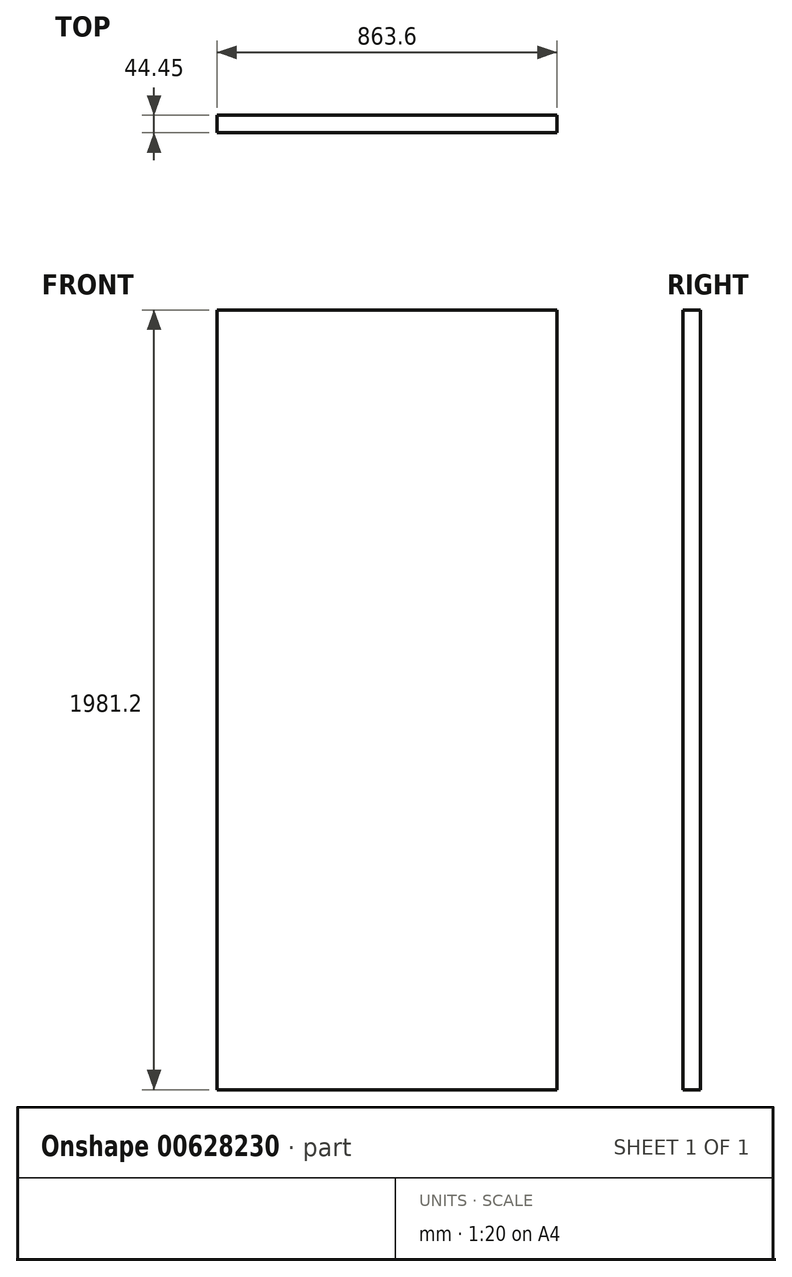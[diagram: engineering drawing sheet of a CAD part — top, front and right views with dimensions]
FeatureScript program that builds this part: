
annotation { "Feature Type Name" : "Feature", "Feature Type Description" : "" }
export const myFeature = defineFeature(function(context is Context, id is Id, definition is map)
    precondition{}
    {
        {
            var Q0;
            Q0=qCreatedBy(makeId("Front.planeOp"),FACE);
            var sketch = newSketch(context, id + "F0", { "sketchPlane" : qUnion([Q0])});
            skLineSegment(sketch, "E0.bottom", {"start": v(0, 0) * mm, "end": v(863.6, 0) * mm});
            skLineSegment(sketch, "E0.top", {"start": v(0, 1981.2) * mm, "end": v(863.6, 1981.2) * mm});
            skLineSegment(sketch, "E0.left", {"start": v(0, 0) * mm, "end": v(0, 1981.2) * mm});
            skLineSegment(sketch, "E0.right", {"start": v(863.6, 0) * mm, "end": v(863.6, 1981.2) * mm});
            skSolve(sketch);
        }
        {
            var Q0;
            Q0 = qSketchRegion(id + "F0", true);
            extrude(context, id + "F1", {"entities" : qUnion([Q0]), "depth" : 44.45 * mm, "offsetDistance" : 25.4 * mm});
        }
    });
